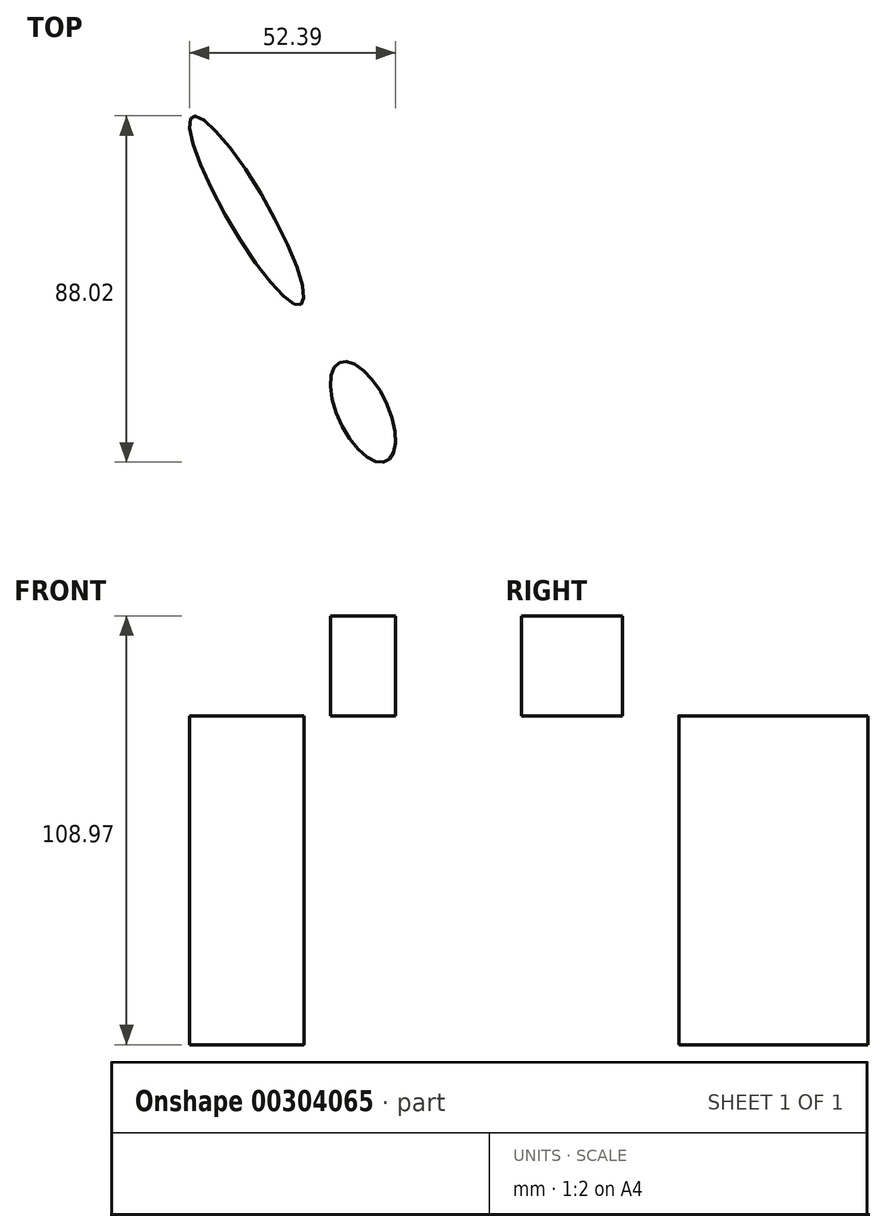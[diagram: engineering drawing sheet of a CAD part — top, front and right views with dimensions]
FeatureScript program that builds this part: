
annotation { "Feature Type Name" : "Feature", "Feature Type Description" : "" }
export const myFeature = defineFeature(function(context is Context, id is Id, definition is map)
    precondition{}
    {
        {
            var Q0;
            Q0=qCreatedBy(makeId("Top.planeOp"),FACE);
            var sketch = newSketch(context, id + "F0", { "sketchPlane" : qUnion([Q0])});
            skEllipse(sketch, "E0", {"center": v(76.1, 75.19) * mm, "majorRadius": 27.6 * mm, "minorRadius": 5.27 * mm, "majorAxis": v(0.5, -0.87)});
            skSolve(sketch);
        }
        {
            var Q0;
            Q0 = qSketchRegion(id + "F0", true);
            extrude(context, id + "F1", {"entities" : qUnion([Q0]), "depth" : 83.57 * mm});
        }
        {
            var Q0;
            Q0=makeQuery(id+"F1.opExtrude","CAP_FACE",FACE,{"disambiguationData":[OSD([sQuery(id+"F0.wireOp",EDGE,"E0")])],"isStart":false});
            var sketch = newSketch(context, id + "F2", { "sketchPlane" : qUnion([Q0])});
            skEllipse(sketch, "E1", {"center": v(105.67, 24.03) * mm, "majorRadius": 13.87 * mm, "minorRadius": 6.36 * mm, "majorAxis": v(-0.43, 0.9)});
            skSolve(sketch);
        }
        {
            var Q0;
            Q0 = qSketchRegion(id + "F2", true);
            extrude(context, id + "F3", {"entities" : qUnion([Q0]), "depth" : 25.4 * mm});
        }
    });
